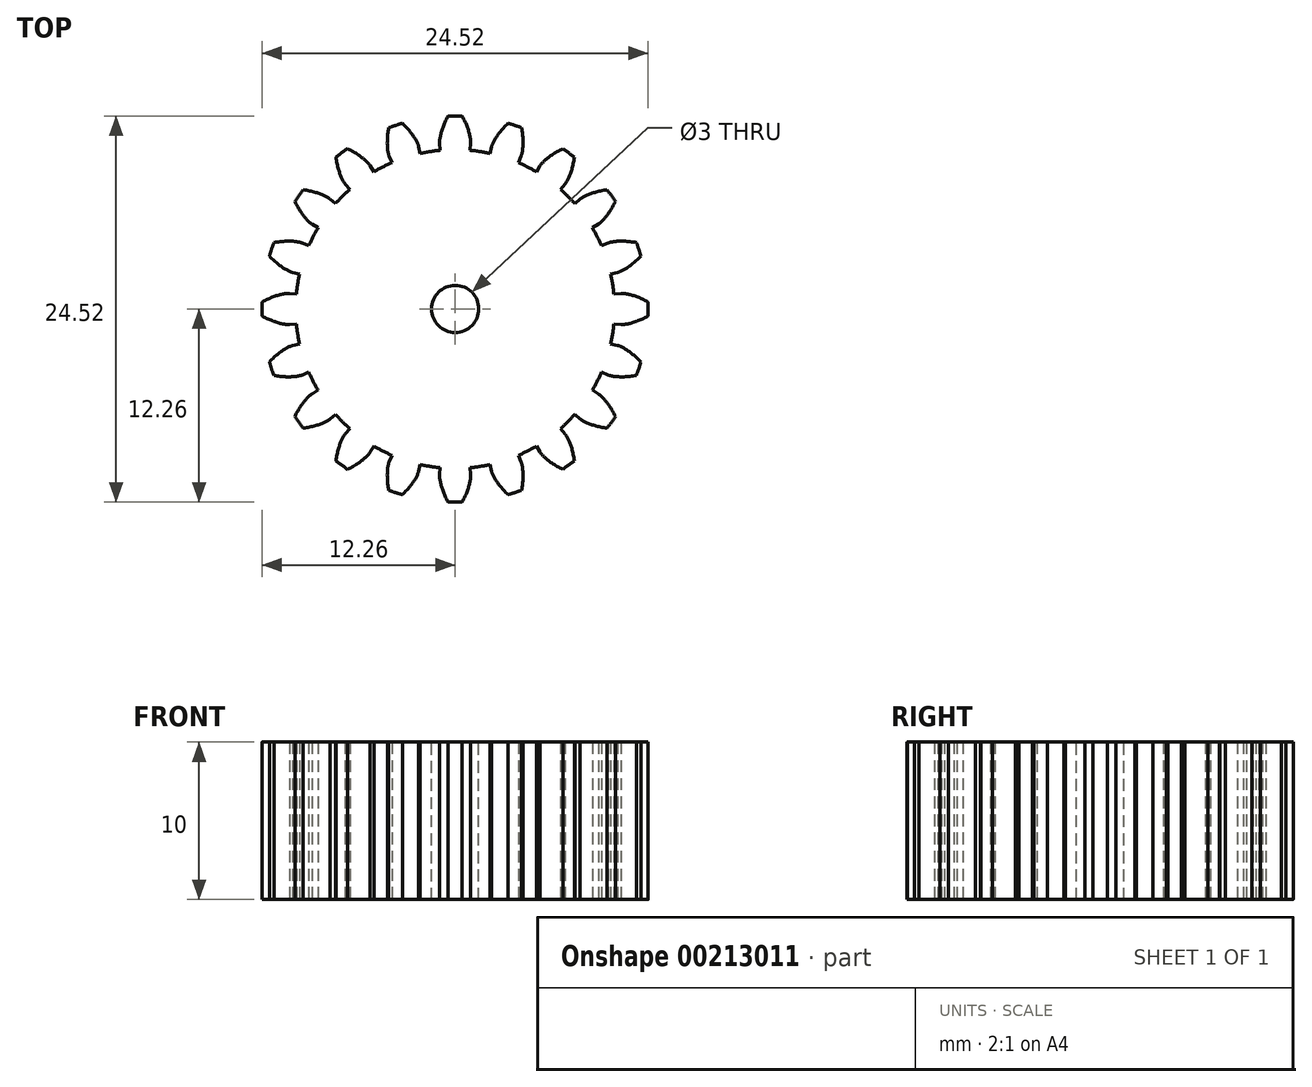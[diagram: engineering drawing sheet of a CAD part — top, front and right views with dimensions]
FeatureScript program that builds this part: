
annotation { "Feature Type Name" : "Feature", "Feature Type Description" : "" }
export const myFeature = defineFeature(function(context is Context, id is Id, definition is map)
    precondition{}
    {
        {
            var Q0;
            Q0=qCreatedBy(makeId("Top.planeOp"),FACE);
            var sketch = newSketch(context, id + "F0", { "sketchPlane" : qUnion([Q0])});
            skCircle(sketch, "E0", {"center": v(0, 0) * mm, "radius": 10.57 * mm, "construction": true});
            skLineSegment(sketch, "E1", {"start": v(10.57, 0) * mm, "end": v(10.57, 0) * mm});
            skLineSegment(sketch, "E2", {"start": v(0, 0) * mm, "end": v(10.55, 0.65) * mm, "construction": true});
            skLineSegment(sketch, "E3", {"start": v(10.55, 0.65) * mm, "end": v(10.6, 0) * mm, "construction": true});
            skLineSegment(sketch, "E4", {"start": v(0, 0) * mm, "end": v(10.5, 1.29) * mm, "construction": true});
            skLineSegment(sketch, "E5", {"start": v(10.5, 1.29) * mm, "end": v(10.65, 0) * mm, "construction": true});
            skLineSegment(sketch, "E6", {"start": v(0, 0) * mm, "end": v(10.4, 1.93) * mm, "construction": true});
            skLineSegment(sketch, "E7", {"start": v(10.4, 1.93) * mm, "end": v(10.75, 0.02) * mm, "construction": true});
            skLineSegment(sketch, "E8", {"start": v(0, 0) * mm, "end": v(10.26, 2.56) * mm, "construction": true});
            skLineSegment(sketch, "E9", {"start": v(10.26, 2.56) * mm, "end": v(10.88, 0.05) * mm, "construction": true});
            skLineSegment(sketch, "E10", {"start": v(0, 0) * mm, "end": v(10.08, 3.18) * mm, "construction": true});
            skLineSegment(sketch, "E11", {"start": v(10.08, 3.18) * mm, "end": v(11.05, 0.1) * mm, "construction": true});
            skLineSegment(sketch, "E12", {"start": v(0, 0) * mm, "end": v(9.87, 3.79) * mm, "construction": true});
            skLineSegment(sketch, "E13", {"start": v(9.87, 3.79) * mm, "end": v(11.26, 0.17) * mm, "construction": true});
            skLineSegment(sketch, "E14", {"start": v(0, 0) * mm, "end": v(9.62, 4.38) * mm, "construction": true});
            skLineSegment(sketch, "E15", {"start": v(9.62, 4.38) * mm, "end": v(11.5, 0.27) * mm, "construction": true});
            skLineSegment(sketch, "E16", {"start": v(0, 0) * mm, "end": v(9.33, 4.96) * mm, "construction": true});
            skLineSegment(sketch, "E17", {"start": v(9.33, 4.96) * mm, "end": v(11.76, 0.4) * mm, "construction": true});
            skLineSegment(sketch, "E18", {"start": v(0, 0) * mm, "end": v(9.01, 5.52) * mm, "construction": true});
            skLineSegment(sketch, "E19", {"start": v(9.01, 5.52) * mm, "end": v(12.05, 0.57) * mm, "construction": true});
            skLineSegment(sketch, "E20", {"start": v(0, 0) * mm, "end": v(8.66, 6.06) * mm, "construction": true});
            skLineSegment(sketch, "E21", {"start": v(8.66, 6.06) * mm, "end": v(12.36, 0.77) * mm, "construction": true});
            skPoint(sketch, "E22", {"position": v(10.57, 0) * mm});
            skCircle(sketch, "E23", {"center": v(0, 0) * mm, "radius": 10.12 * mm});
            skLineSegment(sketch, "E24", {"start": v(10.12, 0) * mm, "end": v(10.57, 0) * mm});
            skFitSpline(sketch, "E25", {"points": [v(10.57, 0) * mm, v(10.6, 0) * mm, v(10.65, 0) * mm, v(10.75, 0.02) * mm, v(10.88, 0.05) * mm, v(11.05, 0.1) * mm, v(11.26, 0.17) * mm, v(11.5, 0.27) * mm, v(11.76, 0.4) * mm, v(12.05, 0.57) * mm, v(12.36, 0.77) * mm], "startDerivative": vector(0.52, 0.01) * mm, "endDerivative": vector(2.16, 1.45) * mm});
            skFitSpline(sketch, "E26", {"points": [v(10.57, 0) * mm, v(10.6, 0) * mm, v(10.65, 0) * mm, v(10.75, 0.02) * mm, v(10.88, 0.05) * mm, v(11.05, 0.1) * mm, v(11.26, 0.17) * mm, v(11.5, 0.27) * mm, v(11.76, 0.4) * mm, v(12.05, 0.57) * mm, v(12.36, 0.77) * mm], "startDerivative": vector(0.52, 0.01) * mm, "endDerivative": vector(2.16, 1.45) * mm, "construction": true});
            skLineSegment(sketch, "E27", {"start": v(0, 0) * mm, "end": v(14, 1.31) * mm, "construction": true});
            skLineSegment(sketch, "E28.MirrorCS", {"start": v(9.95, 1.88) * mm, "end": v(10.39, 1.96) * mm});
            skFitSpline(sketch, "E29.MirrorCS", {"points": [v(10.39, 1.96) * mm, v(10.4, 1.97) * mm, v(10.47, 1.97) * mm, v(10.56, 1.98) * mm, v(10.7, 1.97) * mm, v(10.88, 1.96) * mm, v(11.1, 1.92) * mm, v(11.34, 1.87) * mm, v(11.63, 1.8) * mm, v(11.95, 1.68) * mm, v(12.3, 1.54) * mm], "startDerivative": vector(0.5, 0.08) * mm, "endDerivative": vector(2.39, -1.03) * mm});
            skArc(sketch, "E30", {"start": v(12.16, 1.6) * mm, "mid": v(-12.2, -1.14) * mm, "end": v(12.24, 0.7) * mm, "construction": true});
            skArc(sketch, "E31", {"start": v(12.24, 0.7) * mm, "mid": v(12.2, 1.14) * mm, "end": v(12.16, 1.6) * mm});
            skSolve(sketch);
        }
        {
            var Q0;
            {var subQ0=sQuery(id+"F0.wireOp",EDGE,"E23");var subQ1=makeQuery(id+"F0.imprint","INTERSECT",VERTEX,{"derivedFrom":[subQ0,sQuery(id+"F0.wireOp",EDGE,"E24")]});Q0=makeQuery(id+"F0.imprint","IMPRINT",FACE,{"disambiguationData":[TD([[makeQuery(id+"F0.imprint","IMPRINT",EDGE,{"disambiguationData":[TD([[subQ1,-1.0]])],"derivedFrom":subQ0}),1.0]])]});}
            var Q1;
            {var subQ1=sQuery(id+"F0.wireOp",EDGE,"E24");Q1=makeQuery(id+"F0.imprint","IMPRINT",FACE,{"disambiguationData":[TD([[makeQuery(id+"F0.imprint","IMPRINT",EDGE,{"derivedFrom":subQ1}),1.0]])]});}
            extrude(context, id + "F1", {"entities" : qUnion([Q0, Q1]), "depth" : 10 * mm, "symmetric" : true});
        }
        {
            var Q0;
            Q0=qCreatedBy(makeId("Front.planeOp"),FACE);
            var sketch = newSketch(context, id + "F2", { "sketchPlane" : qUnion([Q0])});
            skLineSegment(sketch, "E32", {"start": v(0, 0) * mm, "end": v(0, 25.35) * mm});
            skSolve(sketch);
        }
        {
            var Q0;
            Q0=makeQuery(id+"F1.opExtrude","CAP_FACE",FACE,{"disambiguationData":[OSD([sQuery(id+"F0.wireOp",EDGE,"E23"),sQuery(id+"F0.wireOp",EDGE,"E24"),sQuery(id+"F0.wireOp",EDGE,"E25"),sQuery(id+"F0.wireOp",EDGE,"E28.MirrorCS"),sQuery(id+"F0.wireOp",EDGE,"E29.MirrorCS"),sQuery(id+"F0.wireOp",EDGE,"E31")])],"isStart":false});
            var sketch = newSketch(context, id + "F3", { "sketchPlane" : qUnion([Q0])});
            skCircle(sketch, "E33", {"center": v(0, 0) * mm, "radius": 1.5 * mm});
            skSolve(sketch);
        }
        {
            var Q0;
            Q0=makeQuery(id+"F1.opExtrude","SWEPT_BODY",BODY,{"disambiguationData":[OSD([sQuery(id+"F0.wireOp",EDGE,"E23"),sQuery(id+"F0.wireOp",EDGE,"E24"),sQuery(id+"F0.wireOp",EDGE,"E25"),sQuery(id+"F0.wireOp",EDGE,"E28.MirrorCS"),sQuery(id+"F0.wireOp",EDGE,"E29.MirrorCS"),sQuery(id+"F0.wireOp",EDGE,"E31")])]});
            var Q1;
            Q1=sQuery(id+"F2.wireOp",EDGE,"E32");
            circularPattern(context, id + "F4", {"operationType" : NewBodyOperationType.ADD, "entities" : qUnion([Q0]), "axis" : qUnion([Q1]), "angle" : 360 * degree, "instanceCount" : 20, "equalSpace" : true});
        }
        {
            var Q0;
            Q0=makeQuery(id+"F3.imprint","IMPRINT",FACE,{"disambiguationData":[TD([[makeQuery(id+"F3.imprint","IMPRINT",EDGE,{"derivedFrom":sQuery(id+"F3.wireOp",EDGE,"E33")}),1.0]])]});
            extrude(context, id + "F5", {"entities" : qUnion([Q0]), "operationType" : NewBodyOperationType.REMOVE, "endBound" : BoundingType.UP_TO_NEXT, "oppositeDirection" : true, "depth" : 25 * mm});
        }
        {
            var Q0;
            Q0=makeQuery(id+"F1.opExtrude","SWEPT_BODY",BODY,{"disambiguationData":[OSD([sQuery(id+"F0.wireOp",EDGE,"E23"),sQuery(id+"F0.wireOp",EDGE,"E24"),sQuery(id+"F0.wireOp",EDGE,"E25"),sQuery(id+"F0.wireOp",EDGE,"E28.MirrorCS"),sQuery(id+"F0.wireOp",EDGE,"E29.MirrorCS"),sQuery(id+"F0.wireOp",EDGE,"E31")])]});
            var Q1;
            Q1=sQuery(id+"F2.wireOp",EDGE,"E32");
            transform(context, id + "F6", {"entities" : qUnion([Q0]), "transformType" : TransformType.ROTATION, "transformAxis" : qUnion([Q1]), "angle" : 5.35 * degree, "oppositeDirection" : true, "makeCopy" : false});
        }
    });
